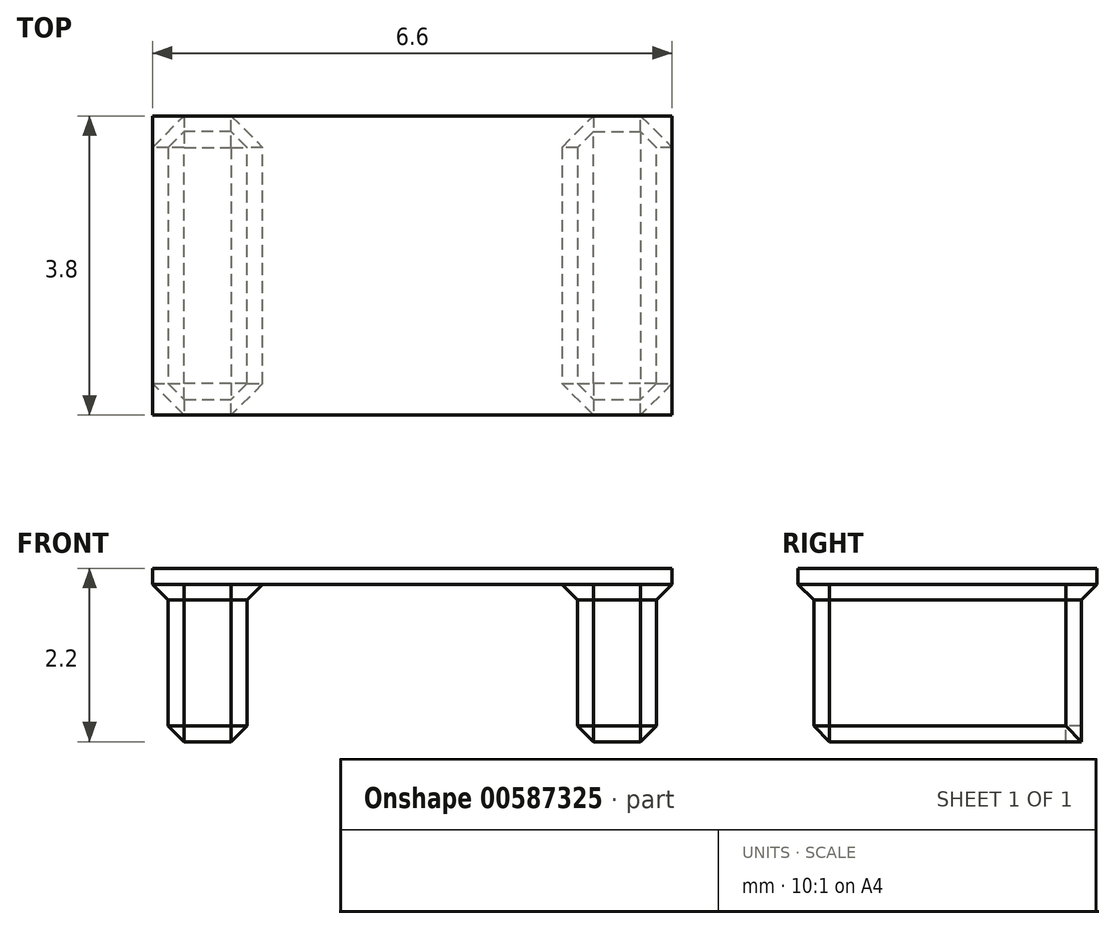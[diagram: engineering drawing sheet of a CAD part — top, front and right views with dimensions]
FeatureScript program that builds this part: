
annotation { "Feature Type Name" : "Feature", "Feature Type Description" : "" }
export const myFeature = defineFeature(function(context is Context, id is Id, definition is map)
    precondition{}
    {
        {
            assignVariable(context, id + "F0", {"name" : "fillet", "anyValue" : 0.2});
        }
        {
            var Q0;
            Q0=qCreatedBy(makeId("Top.planeOp"),FACE);
            var sketch = newSketch(context, id + "F1", { "sketchPlane" : qUnion([Q0])});
            skLineSegment(sketch, "E0.bottom", {"start": v(3.1, -1.73) * mm, "end": v(2.1, -1.73) * mm});
            skLineSegment(sketch, "E0.top", {"start": v(3.1, 1.67) * mm, "end": v(2.1, 1.67) * mm});
            skLineSegment(sketch, "E0.left", {"start": v(3.1, -1.73) * mm, "end": v(3.1, 1.67) * mm});
            skLineSegment(sketch, "E0.right", {"start": v(2.1, -1.73) * mm, "end": v(2.1, 1.67) * mm});
            skPoint(sketch, "E0.middle", {"position": v(2.6, -0.03) * mm});
            skPoint(sketch, "E1.MirrorP", {"position": v(-2.6, -0.03) * mm});
            skLineSegment(sketch, "E2.MirrorCS", {"start": v(-3.1, 1.67) * mm, "end": v(-2.1, 1.67) * mm});
            skLineSegment(sketch, "E3.MirrorCS", {"start": v(-3.1, -1.73) * mm, "end": v(-2.1, -1.73) * mm});
            skLineSegment(sketch, "E4.MirrorCS", {"start": v(-3.1, -1.73) * mm, "end": v(-3.1, 1.67) * mm});
            skLineSegment(sketch, "E5.MirrorCS", {"start": v(-2.1, -1.73) * mm, "end": v(-2.1, 1.67) * mm});
            skLineSegment(sketch, "E6.bottom", {"start": v(-3.3, 1.87) * mm, "end": v(3.3, 1.87) * mm});
            skLineSegment(sketch, "E6.top", {"start": v(-3.3, -1.93) * mm, "end": v(3.3, -1.93) * mm});
            skLineSegment(sketch, "E6.left", {"start": v(-3.3, 1.87) * mm, "end": v(-3.3, -1.93) * mm});
            skLineSegment(sketch, "E6.right", {"start": v(3.3, 1.87) * mm, "end": v(3.3, -1.93) * mm});
            skSolve(sketch);
        }
        {
            var Q0;
            Q0=qCreatedBy(makeId("Right.planeOp"),FACE);
            var sketch = newSketch(context, id + "F2", { "sketchPlane" : qUnion([Q0])});
            skLineSegment(sketch, "E7.bottom", {"start": v(-1.73, 0) * mm, "end": v(1.67, 0) * mm});
            skLineSegment(sketch, "E7.top", {"start": v(-1.73, -2) * mm, "end": v(1.67, -2) * mm});
            skLineSegment(sketch, "E7.left", {"start": v(-1.73, 0) * mm, "end": v(-1.73, -2) * mm});
            skLineSegment(sketch, "E7.right", {"start": v(1.67, 0) * mm, "end": v(1.67, -2) * mm});
            skSolve(sketch);
        }
        {
            var Q0;
            Q0=makeQuery(id+"F1.imprint","IMPRINT",FACE,{"disambiguationData":[TD([[makeQuery(id+"F1.imprint","IMPRINT",EDGE,{"derivedFrom":sQuery(id+"F1.wireOp",EDGE,"E0.bottom")}),1.0]])]});
            var Q1;
            Q1=makeQuery(id+"F1.imprint","IMPRINT",FACE,{"disambiguationData":[TD([[makeQuery(id+"F1.imprint","IMPRINT",EDGE,{"derivedFrom":sQuery(id+"F1.wireOp",EDGE,"E2.MirrorCS")}),-1.0]])]});
            var Q2;
            Q2=makeQuery(id+"F1.imprint","IMPRINT",FACE,{"disambiguationData":[TD([[makeQuery(id+"F1.imprint","IMPRINT",EDGE,{"derivedFrom":sQuery(id+"F1.wireOp",EDGE,"E0.bottom")}),-1.0]])]});
            extrude(context, id + "F3", {"entities" : qUnion([Q0, Q1, Q2]), "depth" : (getVariable(context, 'fillet')) * mm, "offsetDistance" : 25 * mm});
        }
        {
            var Q0;
            Q0=makeQuery(id+"F1.imprint","IMPRINT",FACE,{"disambiguationData":[TD([[makeQuery(id+"F1.imprint","IMPRINT",EDGE,{"derivedFrom":sQuery(id+"F1.wireOp",EDGE,"E2.MirrorCS")}),-1.0]])]});
            var Q1;
            Q1=makeQuery(id+"F1.imprint","IMPRINT",FACE,{"disambiguationData":[TD([[makeQuery(id+"F1.imprint","IMPRINT",EDGE,{"derivedFrom":sQuery(id+"F1.wireOp",EDGE,"E0.bottom")}),-1.0]])]});
            var Q2;
            Q2=sQuery(id+"F2.wireOp",VERTEX,"E7.left.end");
            extrude(context, id + "F4", {"entities" : qUnion([Q0, Q1]), "operationType" : NewBodyOperationType.ADD, "endBound" : BoundingType.UP_TO_VERTEX, "oppositeDirection" : true, "depth" : 25 * mm, "endBoundEntityVertex" : qUnion([Q2]), "offsetDistance" : 25 * mm});
        }
        {
            var Q0;
            Q0=makeQuery(id+"F4.opExtrude","CAP_FACE",FACE,{"disambiguationData":[OSD([dummyQuery(id+"F4.vertexPlane.planeOp",FACE)]),OD(1.0)],"isStart":false});
            var Q1;
            Q1=makeQuery(id+"F4.opExtrude","CAP_FACE",FACE,{"disambiguationData":[OSD([dummyQuery(id+"F4.vertexPlane.planeOp",FACE)]),OD(0.0)],"isStart":false});
            var Q2;
            Q2=makeQuery(id+"F4.opExtrude","SWEPT_FACE",FACE,{"disambiguationData":[OSD([sQuery(id+"F1.wireOp",EDGE,"E3.MirrorCS")])]});
            var Q3;
            Q3=makeQuery(id+"F4.opExtrude","SWEPT_FACE",FACE,{"disambiguationData":[OSD([sQuery(id+"F1.wireOp",EDGE,"E4.MirrorCS")])]});
            var Q4;
            Q4=makeQuery(id+"F4.opExtrude","SWEPT_FACE",FACE,{"disambiguationData":[OSD([sQuery(id+"F1.wireOp",EDGE,"E5.MirrorCS")])]});
            var Q5;
            Q5=makeQuery(id+"F4.opExtrude","SWEPT_FACE",FACE,{"disambiguationData":[OSD([sQuery(id+"F1.wireOp",EDGE,"E2.MirrorCS")])]});
            var Q6;
            Q6=makeQuery(id+"F4.opExtrude","SWEPT_FACE",FACE,{"disambiguationData":[OSD([sQuery(id+"F1.wireOp",EDGE,"E0.left")])]});
            var Q7;
            Q7=makeQuery(id+"F4.opExtrude","SWEPT_FACE",FACE,{"disambiguationData":[OSD([sQuery(id+"F1.wireOp",EDGE,"E0.right")])]});
            var Q8;
            Q8=makeQuery(id+"F4.opExtrude","SWEPT_FACE",FACE,{"disambiguationData":[OSD([sQuery(id+"F1.wireOp",EDGE,"E0.bottom")])]});
            chamfer(context, id + "F5", {"entities" : qUnion([Q0, Q1, Q2, Q3, Q4, Q5, Q6, Q7, Q8]), "width" : (getVariable(context, 'fillet')) * mm, "tangentPropagation" : true});
        }
    });
